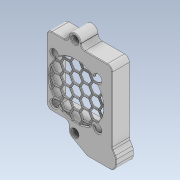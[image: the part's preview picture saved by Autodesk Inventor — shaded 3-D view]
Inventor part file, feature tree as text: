
AUTODESK INVENTOR PART (.ipt)
format: ipt  version: 2022.1 (Build 261234020, 234B)  size: 1,464,320 bytes
history: native  units: mm
features: reference x30, chamfer x13, sketch x13, extrude x12, projected_geometry x6, other x6, fillet x3, plane x2, mirror x2, delete_face x2, hole x2
ambient origin geometry x8: Origin, YZ Plane, XZ Plane, XY Plane, X Axis, Y Axis, Z Axis, Center Point
bodies: Volumenkörper1 (feature_tree)
feature tree (91):
  extrude  "Extrusion1"  Depth=0.3mm
  extrude  "Extrusion2"  Depth=0.3mm
  chamfer  "Fase1"  Distance=11.8mm
  chamfer  "Fase2"  Distance=0.120048mm
  extrude  "Extrusion3"  Depth=1.0mm TaperAngle=0.0deg
  plane  "Arbeitsebene1"
  plane  "Arbeitsebene2"
  mirror  "Spiegeln1"
  mirror  "Spiegeln2"
  extrude  "Extrusion6"  Depth=2.0mm TaperAngle=45.0deg
  chamfer  "Fase3"  Distance=2.0mm Angle=45.0deg
  delete_face  "Fläche löschen5"
  chamfer  "Fase4"  Distance=0.4mm
  chamfer  "Fase5"  [1 undecoded]
  extrude  "Extrusion7"  Depth=2.0mm
  fillet  "Rundung1"  Radius=7.0mm
  extrude  "Extrusion8"  Depth=1.2mm
  extrude  "Extrusion9"  Depth=1.2mm
  extrude  "Extrusion10"  Depth=1.2mm
  sketch  "Skizze11"  dims[d14=5.2mm]
  hole  "Bohrung1"  [1 undecoded]
  chamfer  "Fase6"  Distance=1.2mm
  extrude  "Extrusion11"  Depth=1.2mm
  chamfer  "Fase8"  Distance=1.2mm
  chamfer  "Fase9"  Distance=1.2mm
  delete_face  "Fläche löschen6"
  extrude  "Extrusion12"  Depth=1.2mm
  chamfer  "Fase10"  Distance=1.2mm
  extrude  "Extrusion13"  Depth=2.0mm
  chamfer  "Fase11"  Distance=7.0mm
  extrude  "Extrusion14"  Depth=2.0mm
  hole  "Bohrung2"  [1 undecoded]
  chamfer  "Fase12"  Distance=7.0mm
  fillet  "Rundung2"  Radius=7.0mm
  chamfer  "Fase13"  Distance=7.0mm
  fillet  "Rundung3"  Radius=7.0mm
  chamfer  "Fase14"  Distance=1.2mm
  sketch  "Skizze1"  dims[d0=0.3mm d1=0.3mm]
  reference  "Referenz1"
  reference  "Referenz2"
  reference  "Referenz3"
  reference  "Referenz4"
  reference  "Referenz5"
  reference  "Referenz6"
  reference  "Referenz7"
  reference  "Referenz8"
  reference  "Referenz9"
  reference  "Referenz10"
  reference  "Referenz11"
  reference  "Referenz12"
  reference  "Referenz13"
  reference  "Referenz14"
  reference  "Referenz15"
  reference  "Referenz16"
  reference  "Referenz17"
  sketch  "Skizze2"  dims[d2=0.3mm d3=0.3mm]
  projected_geometry  "Projizierte Kontur1"
  reference  "Referenz18"
  reference  "Referenz19"
  reference  "Referenz20"
  reference  "Referenz21"
  reference  "Referenz22"
  sketch  "Skizze3"  dims[d5=0.3mm]
  sketch  "Skizze4"  dims[d6=1.2mm]
  reference  "Referenz23"
  sketch  "Skizze7"  dims[d7=1.2mm]
  reference  "Referenz24"
  reference  "Referenz25"
  sketch  "Skizze8"  dims[d8=1.2mm]
  reference  "Referenz26"
  projected_geometry  "Projizierte Kontur2"
  sketch  "Skizze9"  dims[d9=1.2mm]
  projected_geometry  "Projizierte Kontur3"
  sketch  "Skizze10"  dims[d11=1.2mm d12=11.8mm d13=0.0mm]
  projected_geometry  "Projizierte Kontur4"
  reference  "Referenz27"
  reference  "Referenz28"
  reference  "Referenz29"
  reference  "Referenz30"
  sketch  "Skizze12"  dims[d15=5.2mm]
  projected_geometry  "Projizierte Kontur5"
  sketch  "Skizze13"  dims[d16=5.2mm]
  projected_geometry  "Projizierte Kontur6"
  sketch  "Skizze14"  dims[d17=5.2mm]
  sketch  "Skizze15"  dims[d19=40.0mm d20=0.120048mm d21=1.0mm d22=0.0mm d23=0.6mm d24=2.0mm d25=45.0deg d26=0.6mm d27=2.0mm d28=45.0deg d29=0.4mm d30=0.0mm d31=0.0mm d32=7.0mm d33=7.0mm d34=7.0mm d35=1.2mm d36=7.0mm d37=7.0mm d38=1.2mm d39=7.0mm d40=7.0mm d41=1.2mm d42=1.2mm d43=1.2mm d44=1.2mm d45=7.0mm d46=7.0mm d47=1.2mm d48=7.0mm d49=7.0mm d50=1.2mm d51=1.2mm d52=1.2mm d53=1.2mm d54=7.0mm d55=1.2mm d56=1.2mm d57=1.2mm d58=1.2mm d59=7.0mm d60=7.0mm d61=1.2mm d62=7.0mm d63=7.0mm d64=1.2mm d65=1.2mm d66=1.2mm d67=1.2mm d68=7.0mm d69=7.0mm d70=1.2mm d71=7.0mm d72=7.0mm d73=1.2mm d74=1.2mm d75=1.2mm d76=1.2mm d77=1.2mm d78=1.2mm d79=1.2mm d80=7.0mm d81=1.2mm d82=7.0mm d104=7.0mm d105=1.2mm d106=7.0mm d107=1.2mm d108=1.2mm d109=1.2mm d111=7.0mm d113=7.0mm d114=7.0mm d115=7.0mm d116=7.0mm d117=7.0mm d118=7.0mm d119=7.0mm d120=7.0mm d121=7.0mm d122=7.0mm d123=7.0mm d124=7.0mm d125=7.0mm d126=1.2mm d127=1.2mm d128=1.2mm d129=1.2mm d131=1.2mm d132=1.2mm d133=1.2mm d134=1.2mm d135=1.2mm d136=1.2mm d137=1.2mm d138=1.2mm d139=1.2mm d140=1.2mm d141=1.2mm d142=1.2mm d143=7.0mm d144=7.0mm d145=1.2mm d146=1.2mm d147=1.2mm d148=1.2mm d151=7.0mm d152=7.0mm d153=7.0mm d154=7.0mm d155=7.0mm d156=7.0mm d157=7.0mm d158=7.0mm d159=7.0mm d162=1.2mm d163=1.2mm d164=1.2mm d165=1.2mm d166=1.2mm d167=7.0mm d168=1.2mm d169=1.2mm d170=7.0mm d171=1.2mm d173=1.2mm d174=1.2mm d175=1.2mm d176=1.2mm d177=7.0mm d178=7.0mm d179=7.0mm d180=7.0mm d181=7.0mm d182=1.2mm d183=1.2mm d184=1.2mm d185=1.2mm d186=1.2mm d187=1.2mm d188=1.2mm d189=1.2mm d190=1.2mm d191=41.2mm d206=1.0mm d207=0.0mm d208=0.4mm d209=2.0mm d210=45.0deg d211=0.4mm d212=2.0mm d213=45.0deg d214=0.4mm d215=2.0mm d216=45.0deg d217=0.889mm d218=2.0mm d219=0.5555mm d220=0.5555mm d221=4.0mm d222=0.0mm d223=1.333333mm d224=4.0mm d225=10.0mm d226=0.0mm d227=1.0mm d228=6.4mm d229=1.2mm d230=1.2mm d231=1.2mm d232=1.2mm d233=4.0mm d234=3.6mm d235=2.4mm d236=10.0mm d237=0.0mm d238=2.0mm d239=0.0mm d240=1.2mm d241=3.0mm d242=4.2mm d244=5.0mm d245=5.0mm d246=3.8mm d247=1.2mm d248=1.2mm d249=3.0mm d250=4.2mm d251=5.6mm d252=1.6mm d253=1.2mm d254=4.2mm d255=3.0mm d256=1.0mm d257=1.2mm d258=10.0mm d259=0.0mm d260=3.4mm d261=6.0mm d262=5.6mm d263=5.0mm d264=90.0deg d265=8.0mm d266=20.594885mm d267=0.55mm d268=2.0mm d269=45.0deg d270=2.0mm d271=0.0mm d275=1.0mm d276=2.0mm d277=45.0deg d278=0.4mm d279=2.0mm d280=45.0deg d281=1.0mm d282=1.0mm d283=1.0mm d284=1.0mm d286=1.0mm d287=1.0mm d289=1.0mm d291=1.0mm d292=0.2mm d293=0.0mm d294=1.0mm d295=2.0mm d296=45.0deg d297=2.0mm d298=15.0mm d299=1.2mm d300=0.0mm d301=1.0mm d302=2.0mm d303=45.0deg d304=6.4mm d305=6.4mm d306=1.2mm d307=0.0mm d308=1.2mm d309=0.0mm d310=3.4mm d311=6.0mm d312=5.6mm d313=5.0mm d314=90.0deg d315=8.0mm d316=20.594885mm d317=0.4mm d318=2.0mm d319=45.0deg d320=3.0mm d321=0.55mm d322=2.0mm d323=45.0deg d324=3.0mm d325=0.4mm d326=2.0mm d327=45.0deg]
  other  "<userpath>\Desktop\GitHub\Voron-2-Mods\Arducam_IMX477_CM4\CM4\CAD\CM4_Case.iam"
  other  "CM4_Case.iam"
  other  "Noctua-Fan-NF-A4x10_40mm:1"
  other  "Noctua-NF-A4x10 v1:1"
  other  "Noctua nf-a8-pwm fan 40x40x10 v2:1"
  other  "CM4_Case_Top:1"
note: 3 required parameter values undecoded (feature->parameter linkage not recoverable at this tier; creation-order binding heuristic only, values carry confidence <= 0.55)
